# Revit family: NBS_DudleyIndustries_SoapDpnsrs_PlasmaRange_SoapDispenser1Litre
name_source: partatom
category: Specialty Equipment
revit_build: Autodesk Revit 2016 (Build: 20150220_1215(x64)
units: mm (PartAtom-declared; Revit-internal decimal feet)

## family parameters
Cut with Voids When Loaded = No
Host = Face
OmniClass Number = 23.40.20.21.34
OmniClass Title = Soap Holders, Dispensers
Part Type = Normal
Room Calculation Point = No
Round Connector Dimension = Use Diameter
Shared = No

## types (1)
- PlasmaRangeSoapDispenser1Litre
    AssetType = Fixed
    BIMObjectName = NBS_DudleyIndustries_SoapDispensers_PlasmaRange_SoapDispenser1Litre
    Category = Pr_40_70_22_81:Soap dispensers
    Color = Stainless steel, White
    Default Elevation = 1200 mm
    Description = 1 Litre Soap Dispenser
    DispenserCaseMaterial = NBS_Concept
    DispenserLockMaterial = NBS_Concept
    DurationUnit = year
    ExpectedLife = 5
    Finish = Brushed (50440SS), Polished (50440PS)
    Form = Wall mounted
    IfcExportAs = IfcFurnitureType
    IfcExportType = NOTDEFINED
    MainColor = Stainless Steel
    ManufacturerName = Dudley Industries
    ManufacturerURL = www.dudleyindustries.com/
    Material = Stainless Steel
    MaterialsBody = Stainless Steel
    MaterialsFinishColour = Brushed (50300SS), Polished (50300PS), Coated (50300CB), White Powder Coated (50300WH)
    ModelNumber = 50300
    ModelReference = Plasma Range: Soap Dispenser 1 Litre
    NBSCertification = www.nationalbimlibrary.com/cert/0zgvse25
    NBSDescription = Soap dispensers
    NBSReference = 45-35-72/358
    Name = SoapDispensers_PlasmaRange:SoapDispenser1Litre_DudleyIndustries
    NominalDepth = 95 mm
    NominalHeight = 269 mm  [stored 0.882546 ft]
    NominalLength = 101 mm  [stored 0.331365 ft]
    NominalWidth = 101 mm  [stored 0.331365 ft]
    Operation = Manual push operation
    ProductInformation = www.dudleyindustries.com/wp-content/uploads/2016/11/1-Litre-Soap-Dispenser-1.pdf
    Size = 112 x 250 x 93 mm
    Style = Soap dispenser
    Uniclass2015Code = Pr_40_70_22_81
    Uniclass2015Title = Soap dispensers
    Uniclass2015Version = Products v1.7
    Version = 2
    WarrantyDescription = 1 year warranty
    WarrantyDurationParts = 1
    WarrantyDurationUnit = year

note: [stored X ft] marks values corroborated as IEEE doubles in the binary element streams (Revit-internal decimal feet)

## geometry (parser evidence)
native form markers: Sweep x2
no freeform markers — native parametric forms only
